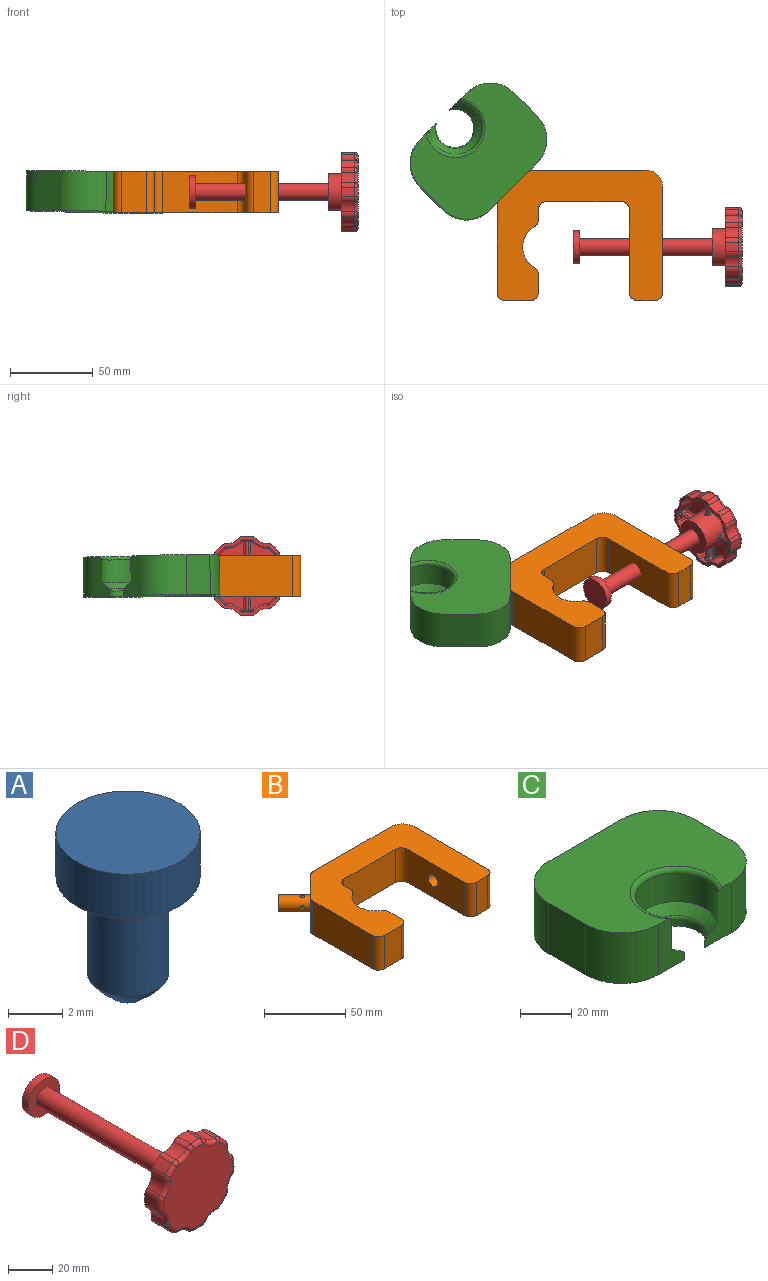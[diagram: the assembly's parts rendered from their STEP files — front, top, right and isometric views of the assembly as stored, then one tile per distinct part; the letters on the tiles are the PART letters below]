
ASSEMBLY  parts=4 mates=4
PART A: 6 faces, bbox 5.3x5.3x7.3 mm
  f0: cylinder r=1.5mm len=4.3mm, axis (0,0,-1), area 40.5mm2, adj f3,f5
  f1: cylinder r=2.65mm len=5.3mm, axis (0,0,-1), area 33.3mm2, adj f2,f3
  f2: plane 5.3x5.3mm, normal (0,0,1), area 22.1mm2, adj f1
  f3: plane 5.3x5.3mm, normal (0,0,-1), area 15mm2, adj f0,f1
  f4: plane 1.01x1.01mm, normal (0,0,-1), area 0.8mm2, adj f5
  f5: bspline ~3x3mm, area 9.3mm2, adj f0,f4
PART B: 35 faces, bbox 107.7x86.7x25 mm
  f0: cylinder r=5mm len=21.21mm, axis (0.71,-0.71,0), area 603.4mm2, adj f22,f23,f25,f27,f29,f31
  f1: plane 100x79mm, normal (0,0,-1), area 4176.6mm2, adj f2,f4,f5,f6,f7,f8,f9,f10
  f2: plane 51.93x25mm, normal (-1,0,0), area 1298.2mm2, adj f1,f3,f18,f34
  f3: plane 100x79mm, normal (0,0,1), area 4176.6mm2, adj f2,f4,f5,f6,f7,f8,f9,f10
  f4: plane 67.93x25mm, normal (0,1,0), area 1698.2mm2, adj f1,f3,f32,f33
  f5: plane 64x25mm, normal (1,0,0), area 1543.3mm2, adj f1,f3,f19,f21,f32
  f6: plane 25x10mm, normal (0,-1,0), area 250mm2, adj f1,f3,f20,f21
  f7: plane 25x15mm, normal (0,-1,0), area 375mm2, adj f1,f3,f17,f18
  f8: plane 50x25mm, normal (-1,0,0), area 1193.3mm2, adj f1,f3,f13,f19,f20
  f9: plane 45x25mm, normal (0,-1,0), area 1125mm2, adj f1,f3,f13,f14
  f10: plane 25x5.85mm, normal (1,0,0), area 146.2mm2, adj f1,f3,f14,f15
  f11: cylinder r=14.34mm len=25mm, axis (0,0,1), area 743.7mm2, adj f1,f3,f15,f16
  f12: plane 25x10.85mm, normal (1,0,0), area 271.2mm2, adj f1,f3,f16,f17
  f13: cylinder r=5mm len=25mm, axis (0,0,1), area 196.3mm2, adj f1,f3,f8,f9
  f14: cylinder r=5mm len=25mm, axis (0,0,1), area 196.3mm2, adj f1,f3,f9,f10
  f15: cylinder r=5mm len=25mm, axis (0,0,1), area 129.7mm2, adj f1,f3,f10,f11
  f16: cylinder r=5mm len=25mm, axis (0,0,1), area 129.7mm2, adj f1,f3,f11,f12
  f17: cylinder r=5mm len=25mm, axis (0,0,-1), area 196.3mm2, adj f1,f3,f7,f12
  f18: cylinder r=5mm len=25mm, axis (0,0,-1), area 196.3mm2, adj f1,f2,f3,f7
  f19: cylinder r=4.25mm len=20mm, axis (1,0,0), area 534.1mm2, adj f5,f8
  f20: cylinder r=5mm len=25mm, axis (0,0,1), area 196.3mm2, adj f1,f3,f6,f8
  f21: cylinder r=5mm len=25mm, axis (0,0,1), area 196.3mm2, adj f1,f3,f5,f6
  f22: plane 25x17.07mm, normal (-0.71,0.71,0), area 525mm2, adj f0,f1,f3,f33,f34
  f23: plane 10x7.07mm, normal (-0.71,0.71,0), area 78.5mm2, adj f0
  f24: plane 0.5x0.5mm, normal (0,0,1), area 0.2mm2, adj f25
  f25: bspline ~2.85x2.85mm, area 6.5mm2, adj f0,f24
  f26: plane 0.5x0.35mm, normal (-0.71,-0.71,0), area 0.2mm2, adj f27
  f27: bspline ~3.88x3.33mm, area 6.8mm2, adj f0,f26
  f28: plane 0.5x0.5mm, normal (0,0,-1), area 0.2mm2, adj f29
  f29: bspline ~2.96x2.96mm, area 6.8mm2, adj f0,f28
  f30: plane 0.5x0.36mm, normal (0.71,0.71,0), area 0.2mm2, adj f31
  f31: bspline ~2.96x2.11mm, area 7.9mm2, adj f0,f30
  f32: cylinder r=10mm len=25mm, axis (0,0,1), area 392.7mm2, adj f1,f3,f4,f5
  f33: cylinder r=5mm len=25mm, axis (0,0,1), area 98.2mm2, adj f1,f3,f4,f22
  f34: cylinder r=5mm len=25mm, axis (0,0,-1), area 98.2mm2, adj f1,f2,f3,f22
PART C: 21 faces, bbox 80x63.2x24 mm
  f0: cylinder r=1.65mm len=5.02mm, axis (0,0,-1), area 50.6mm2, adj f1,f20
  f1: cylinder r=5.25mm len=20mm, axis (0,1,0), area 651.1mm2, adj f0,f6,f16
  f2: plane 24x14.32mm, normal (0,-1,0), area 220.5mm2, adj f7,f8,f9,f10,f12,f13,f14,f15
  f3: plane 24x20mm, normal (-1,0,0), area 480mm2, adj f8,f12,f15,f17
  f4: plane 24x20mm, normal (1,0,0), area 480mm2, adj f8,f11,f15,f18
  f5: plane 24x14.32mm, normal (0,-1,0), area 220.5mm2, adj f7,f8,f9,f10,f11,f13,f14,f15
  f6: plane 40x24mm, normal (0,1,0), area 873.4mm2, adj f1,f8,f15,f17,f18
  f7: cylinder r=11.5mm len=23mm, axis (0,0,1), area 191.5mm2, adj f2,f5,f14,f15
  f8: plane 80x60mm, normal (0,0,1), area 3607.2mm2, adj f2,f3,f4,f5,f6,f11,f12,f13
  f9: cylinder r=16mm len=32mm, axis (0,0,1), area 970.2mm2, adj f2,f5,f10,f13
  f10: cone r=11.5mm half-angle=45deg, axis (0,0,1), area 368mm2, adj f2,f5,f9,f14
  f11: cylinder r=20mm len=24mm, axis (0,0,-1), area 754mm2, adj f4,f5,f8,f15
  f12: cylinder r=20mm len=24mm, axis (0,0,1), area 754mm2, adj f2,f3,f8,f15
  f13: torus R=18mm, axis (0,0,1), area 232.5mm2, adj f2,f5,f8,f9
  f14: torus R=13.5mm, axis (0,0,-1), area 95.4mm2, adj f2,f5,f7,f10
  f15: plane 80x60mm, normal (0,0,-1), area 4030.6mm2, adj f2,f3,f4,f5,f6,f7,f11,f12
  f16: plane 10.5x10.5mm, normal (0,1,0), area 86.6mm2, adj f1
  f17: cylinder r=20mm len=24mm, axis (0,0,-1), area 754mm2, adj f3,f6,f8,f15
  f18: cylinder r=20mm len=24mm, axis (0,0,1), area 754mm2, adj f4,f6,f8,f15
  f19: cylinder r=2.65mm len=5.3mm, axis (0,0,-1), area 33.3mm2, adj f15,f20
  f20: plane 5.3x5.3mm, normal (0,0,-1), area 13.5mm2, adj f0,f19
PART D: 219 faces, bbox 48.4x102x48.4 mm
  f0: plane 18.9x18.9mm, normal (0,1,0), area 169.4mm2, adj f128,f129,f130,f131,f132,f133,f134,f135
  f1: cylinder r=22mm len=7mm, axis (0,1,0), area 18.7mm2, adj f7,f92,f93,f135,f145,f171,f172,f173
  f2: cylinder r=22mm len=7mm, axis (0,1,0), area 18.7mm2, adj f7,f96,f97,f120,f136,f165,f166,f167
  f3: plane 18.9x18.9mm, normal (0,1,0), area 169.4mm2, adj f140,f141,f142,f143,f144,f145,f146,f147
  f4: cylinder r=22mm len=7mm, axis (0,1,0), area 18.7mm2, adj f7,f98,f99,f127,f159,f177,f178,f179
  f5: plane 18.9x18.9mm, normal (0,1,0), area 169.4mm2, adj f152,f153,f154,f155,f156,f157,f158,f159
  f6: cylinder r=22mm len=7mm, axis (0,1,0), area 18.7mm2, adj f7,f88,f89,f150,f160,f207,f208,f209
  f7: plane 48x48mm, normal (0,1,0), area 293.1mm2, adj f1,f2,f4,f6,f8,f9,f10,f11
  f8: cylinder r=8mm len=8mm, axis (0,1,0), area 58.9mm2, adj f7,f34,f35,f67
  f9: cylinder r=24mm len=8mm, axis (0,1,0), area 47.1mm2, adj f7,f33,f34,f63
  f10: cylinder r=8mm len=8mm, axis (0,1,0), area 58.9mm2, adj f7,f32,f33,f59
  f11: cylinder r=24mm len=8mm, axis (0,1,0), area 47.1mm2, adj f7,f31,f32,f55
  f12: cylinder r=8mm len=8mm, axis (0,1,0), area 58.9mm2, adj f7,f30,f31,f51
  f13: cylinder r=24mm len=8mm, axis (0,1,0), area 47.1mm2, adj f7,f29,f30,f47
  f14: cylinder r=8mm len=8mm, axis (0,1,0), area 58.9mm2, adj f7,f28,f29,f43
  f15: cylinder r=24mm len=8mm, axis (0,1,0), area 47.1mm2, adj f7,f27,f28,f42
  f16: cylinder r=8mm len=8mm, axis (0,1,0), area 58.9mm2, adj f7,f26,f27,f46
  f17: cylinder r=24mm len=8mm, axis (0,1,0), area 47.1mm2, adj f7,f25,f26,f50
  f18: cylinder r=8mm len=8mm, axis (0,1,0), area 58.9mm2, adj f7,f25,f37,f54
  f19: cylinder r=24mm len=8mm, axis (0,1,0), area 47.1mm2, adj f7,f37,f38,f58
  f20: cylinder r=8mm len=8mm, axis (0,1,0), area 58.9mm2, adj f7,f38,f39,f62
  f21: cylinder r=24mm len=8mm, axis (0,1,0), area 47.1mm2, adj f7,f39,f40,f66
  f22: cylinder r=8mm len=8mm, axis (0,1,0), area 58.9mm2, adj f7,f36,f40,f70
  f23: cylinder r=24mm len=8mm, axis (0,1,0), area 47.1mm2, adj f7,f35,f36,f71
  f24: plane 44x44mm, normal (0,-1,0), area 1411.4mm2, adj f41,f42,f43,f44,f45,f46,f47,f48
  f25: cylinder r=4mm len=8mm, axis (0,-1,0), area 23.4mm2, adj f7,f17,f18,f52
  f26: cylinder r=4mm len=8mm, axis (0,-1,0), area 23.4mm2, adj f7,f16,f17,f48
  f27: cylinder r=4mm len=8mm, axis (0,-1,0), area 23.4mm2, adj f7,f15,f16,f44
  f28: cylinder r=4mm len=8mm, axis (0,-1,0), area 23.4mm2, adj f7,f14,f15,f41
  f29: cylinder r=4mm len=8mm, axis (0,-1,0), area 23.4mm2, adj f7,f13,f14,f45
  f30: cylinder r=4mm len=8mm, axis (0,-1,0), area 23.4mm2, adj f7,f12,f13,f49
  f31: cylinder r=4mm len=8mm, axis (0,-1,0), area 23.4mm2, adj f7,f11,f12,f53
  f32: cylinder r=4mm len=8mm, axis (0,-1,0), area 23.4mm2, adj f7,f10,f11,f57
  f33: cylinder r=4mm len=8mm, axis (0,-1,0), area 23.4mm2, adj f7,f9,f10,f61
  f34: cylinder r=4mm len=8mm, axis (0,-1,0), area 23.4mm2, adj f7,f8,f9,f65
  f35: cylinder r=4mm len=8mm, axis (0,-1,0), area 23.4mm2, adj f7,f8,f23,f69
  f36: cylinder r=4mm len=8mm, axis (0,-1,0), area 23.4mm2, adj f7,f22,f23,f72
  f37: cylinder r=4mm len=8mm, axis (0,-1,0), area 23.4mm2, adj f7,f18,f19,f56
  f38: cylinder r=4mm len=8mm, axis (0,-1,0), area 23.4mm2, adj f7,f19,f20,f60
  f39: cylinder r=4mm len=8mm, axis (0,-1,0), area 23.4mm2, adj f7,f20,f21,f64
  f40: cylinder r=4mm len=8mm, axis (0,-1,0), area 23.4mm2, adj f7,f21,f22,f68
  f41: torus R=2mm, axis (0,1,0), area 7.5mm2, adj f24,f28,f42,f43
  f42: torus R=22mm, axis (0,1,0), area 18mm2, adj f15,f24,f41,f44
  f43: torus R=10mm, axis (0,1,0), area 25.3mm2, adj f14,f24,f41,f45
  f44: torus R=2mm, axis (0,1,0), area 7.5mm2, adj f24,f27,f42,f46
  f45: torus R=2mm, axis (0,1,0), area 7.5mm2, adj f24,f29,f43,f47
  f46: torus R=10mm, axis (0,1,0), area 25.3mm2, adj f16,f24,f44,f48
  f47: torus R=22mm, axis (0,1,0), area 18mm2, adj f13,f24,f45,f49
  f48: torus R=2mm, axis (0,1,0), area 7.5mm2, adj f24,f26,f46,f50
  f49: torus R=2mm, axis (0,1,0), area 7.5mm2, adj f24,f30,f47,f51
  f50: torus R=22mm, axis (0,1,0), area 18mm2, adj f17,f24,f48,f52
  f51: torus R=10mm, axis (0,1,0), area 25.3mm2, adj f12,f24,f49,f53
  f52: torus R=2mm, axis (0,1,0), area 7.5mm2, adj f24,f25,f50,f54
  f53: torus R=2mm, axis (0,1,0), area 7.5mm2, adj f24,f31,f51,f55
  f54: torus R=10mm, axis (0,1,0), area 25.3mm2, adj f18,f24,f52,f56
  f55: torus R=22mm, axis (0,1,0), area 18mm2, adj f11,f24,f53,f57
  f56: torus R=2mm, axis (0,1,0), area 7.5mm2, adj f24,f37,f54,f58
  f57: torus R=2mm, axis (0,1,0), area 7.5mm2, adj f24,f32,f55,f59
  f58: torus R=22mm, axis (0,1,0), area 18mm2, adj f19,f24,f56,f60
  f59: torus R=10mm, axis (0,1,0), area 25.3mm2, adj f10,f24,f57,f61
  f60: torus R=2mm, axis (0,1,0), area 7.5mm2, adj f24,f38,f58,f62
  f61: torus R=2mm, axis (0,1,0), area 7.5mm2, adj f24,f33,f59,f63
  f62: torus R=10mm, axis (0,1,0), area 25.3mm2, adj f20,f24,f60,f64
  f63: torus R=22mm, axis (0,1,0), area 18mm2, adj f9,f24,f61,f65
  f64: torus R=2mm, axis (0,1,0), area 7.5mm2, adj f24,f39,f62,f66
  f65: torus R=2mm, axis (0,1,0), area 7.5mm2, adj f24,f34,f63,f67
  f66: torus R=22mm, axis (0,1,0), area 18mm2, adj f21,f24,f64,f68
  f67: torus R=10mm, axis (0,1,0), area 25.3mm2, adj f8,f24,f65,f69
  f68: torus R=2mm, axis (0,1,0), area 7.5mm2, adj f24,f40,f66,f70
  f69: torus R=2mm, axis (0,1,0), area 7.5mm2, adj f24,f35,f67,f71
  f70: torus R=10mm, axis (0,1,0), area 25.3mm2, adj f22,f24,f68,f72
  f71: torus R=22mm, axis (0,1,0), area 18mm2, adj f23,f24,f69,f72
  f72: torus R=2mm, axis (0,1,0), area 7.5mm2, adj f24,f36,f70,f71
  f73: cylinder r=10mm len=8.21mm, axis (0,1,0), area 64.5mm2, adj f7,f95,f96,f132
  f74: cylinder r=22mm len=7mm, axis (0,1,0), area 37.8mm2, adj f7,f94,f95,f128
  f75: cylinder r=10mm len=8.21mm, axis (0,1,0), area 64.5mm2, adj f7,f93,f94,f131
  f76: cylinder r=10mm len=8.21mm, axis (0,1,0), area 64.5mm2, adj f7,f91,f92,f141
  f77: cylinder r=22mm len=7mm, axis (0,1,0), area 37.8mm2, adj f7,f90,f91,f142
  f78: cylinder r=10mm len=8.21mm, axis (0,1,0), area 64.5mm2, adj f7,f89,f90,f146
  f79: cylinder r=10mm len=8.21mm, axis (0,1,0), area 64.5mm2, adj f7,f87,f88,f156
  f80: cylinder r=22mm len=7mm, axis (0,1,0), area 37.8mm2, adj f7,f86,f87,f152
  f81: cylinder r=10mm len=8.21mm, axis (0,1,0), area 64.5mm2, adj f7,f86,f98,f155
  f82: cylinder r=10mm len=8.21mm, axis (0,1,0), area 64.5mm2, adj f7,f99,f100,f123
  f83: cylinder r=22mm len=7mm, axis (0,1,0), area 37.8mm2, adj f7,f100,f101,f119
  f84: cylinder r=10mm len=8.21mm, axis (0,1,0), area 64.5mm2, adj f7,f97,f101,f116
  f85: plane 18.9x18.9mm, normal (0,1,0), area 169.4mm2, adj f116,f117,f118,f119,f120,f121,f122,f123
  f86: cylinder r=2mm len=7mm, axis (0,-1,0), area 10.2mm2, adj f7,f80,f81,f153
  f87: cylinder r=2mm len=7mm, axis (0,-1,0), area 10.2mm2, adj f7,f79,f80,f154
  f88: cylinder r=2mm len=7mm, axis (0,-1,0), area 10.2mm2, adj f6,f7,f79,f158
  f89: cylinder r=2mm len=7mm, axis (0,-1,0), area 10.2mm2, adj f6,f7,f78,f148
  f90: cylinder r=2mm len=7mm, axis (0,-1,0), area 10.2mm2, adj f7,f77,f78,f144
  f91: cylinder r=2mm len=7mm, axis (0,-1,0), area 10.2mm2, adj f7,f76,f77,f140
  f92: cylinder r=2mm len=7mm, axis (0,-1,0), area 10.2mm2, adj f1,f7,f76,f143
  f93: cylinder r=2mm len=7mm, axis (0,-1,0), area 10.2mm2, adj f1,f7,f75,f133
  f94: cylinder r=2mm len=7mm, axis (0,-1,0), area 10.2mm2, adj f7,f74,f75,f129
  f95: cylinder r=2mm len=7mm, axis (0,-1,0), area 10.2mm2, adj f7,f73,f74,f130
  f96: cylinder r=2mm len=7mm, axis (0,-1,0), area 10.2mm2, adj f2,f7,f73,f134
  f97: cylinder r=2mm len=7mm, axis (0,-1,0), area 10.2mm2, adj f2,f7,f84,f118
  f98: cylinder r=2mm len=7mm, axis (0,-1,0), area 10.2mm2, adj f4,f7,f81,f157
  f99: cylinder r=2mm len=7mm, axis (0,-1,0), area 10.2mm2, adj f4,f7,f82,f125
  f100: cylinder r=2mm len=7mm, axis (0,-1,0), area 10.2mm2, adj f7,f82,f83,f121
  f101: cylinder r=2mm len=7mm, axis (0,-1,0), area 10.2mm2, adj f7,f83,f84,f117
  f102: plane 22x22mm, normal (0,1,0), area 301.6mm2, adj f103,f212
  f103: cylinder r=11mm len=22mm, axis (0,-1,0), area 977.8mm2, adj f102,f124,f139,f149,f163,f183,f184,f185
  f104: plane 9.07x3mm, normal (0,0,1), area 27.2mm2, adj f113,f162,f204,f207
  f105: plane 9.07x3mm, normal (0,0,-1), area 27.2mm2, adj f113,f151,f201,f210
  f106: plane 9.07x3mm, normal (-1,0,0), area 27.2mm2, adj f115,f126,f177,f186
  f107: plane 9.07x3mm, normal (1,0,0), area 27.2mm2, adj f115,f161,f180,f183
  f108: plane 9.07x3mm, normal (0,0,-1), area 27.2mm2, adj f112,f138,f165,f192
  f109: plane 9.07x3mm, normal (0,0,1), area 27.2mm2, adj f112,f122,f168,f189
  f110: plane 9.07x3mm, normal (1,0,0), area 27.2mm2, adj f114,f147,f171,f198
  f111: plane 9.07x3mm, normal (-1,0,0), area 27.2mm2, adj f114,f137,f174,f195
  f112: cylinder r=1mm len=9.17mm, axis (1,0,0), area 28.4mm2, adj f108,f109,f166,f167,f190,f191
  f113: cylinder r=1mm len=9.17mm, axis (-1,0,0), area 28.4mm2, adj f104,f105,f202,f203,f208,f209
  f114: cylinder r=1mm len=9.17mm, axis (0,0,1), area 28.4mm2, adj f110,f111,f172,f173,f196,f197
  f115: cylinder r=1mm len=9.17mm, axis (0,0,-1), area 28.4mm2, adj f106,f107,f178,f179,f184,f185
  f116: torus R=11mm, axis (0,1,0), area 15mm2, adj f84,f85,f117,f118
  f117: torus R=1mm, axis (0,1,0), area 1.9mm2, adj f85,f101,f116,f119
  f118: torus R=1mm, axis (0,1,0), area 1.9mm2, adj f85,f97,f116,f120
  f119: torus R=21mm, axis (0,1,0), area 8.3mm2, adj f83,f85,f117,f121
  f120: torus R=21mm, axis (0,1,0), area 0.9mm2, adj f2,f85,f118,f169
  f121: torus R=1mm, axis (0,1,0), area 1.9mm2, adj f85,f100,f119,f123
  f122: cylinder r=1mm len=9.07mm, axis (-1,0,0), area 14.3mm2, adj f85,f109,f169,f188
  f123: torus R=11mm, axis (0,1,0), area 15mm2, adj f82,f85,f121,f125
  f124: torus R=12mm, axis (0,1,0), area 22.1mm2, adj f85,f103,f187,f188
  f125: torus R=1mm, axis (0,1,0), area 1.9mm2, adj f85,f99,f123,f127
  f126: cylinder r=1mm len=9.07mm, axis (0,0,-1), area 14.3mm2, adj f85,f106,f176,f187
  f127: torus R=21mm, axis (0,1,0), area 0.9mm2, adj f4,f85,f125,f176
  f128: torus R=21mm, axis (0,1,0), area 8.3mm2, adj f0,f74,f129,f130
  f129: torus R=1mm, axis (0,1,0), area 1.9mm2, adj f0,f94,f128,f131
  f130: torus R=1mm, axis (0,1,0), area 1.9mm2, adj f0,f95,f128,f132
  f131: torus R=11mm, axis (0,1,0), area 15mm2, adj f0,f75,f129,f133
  f132: torus R=11mm, axis (0,1,0), area 15mm2, adj f0,f73,f130,f134
  f133: torus R=1mm, axis (0,1,0), area 1.9mm2, adj f0,f93,f131,f135
  f134: torus R=1mm, axis (0,1,0), area 1.9mm2, adj f0,f96,f132,f136
  f135: torus R=21mm, axis (0,1,0), area 0.9mm2, adj f0,f1,f133,f175
  f136: torus R=21mm, axis (0,1,0), area 0.9mm2, adj f0,f2,f134,f164
  f137: cylinder r=1mm len=9.07mm, axis (0,0,1), area 14.3mm2, adj f0,f111,f175,f194
  f138: cylinder r=1mm len=9.07mm, axis (-1,0,0), area 14.3mm2, adj f0,f108,f164,f193
  f139: torus R=12mm, axis (0,1,0), area 22.1mm2, adj f0,f103,f193,f194
  f140: torus R=1mm, axis (0,1,0), area 1.9mm2, adj f3,f91,f141,f142
  f141: torus R=11mm, axis (0,1,0), area 15mm2, adj f3,f76,f140,f143
  f142: torus R=21mm, axis (0,1,0), area 8.3mm2, adj f3,f77,f140,f144
  f143: torus R=1mm, axis (0,1,0), area 1.9mm2, adj f3,f92,f141,f145
  f144: torus R=1mm, axis (0,1,0), area 1.9mm2, adj f3,f90,f142,f146
  f145: torus R=21mm, axis (0,1,0), area 0.9mm2, adj f1,f3,f143,f170
  f146: torus R=11mm, axis (0,1,0), area 15mm2, adj f3,f78,f144,f148
  f147: cylinder r=1mm len=9.07mm, axis (0,0,-1), area 14.3mm2, adj f3,f110,f170,f199
  f148: torus R=1mm, axis (0,1,0), area 1.9mm2, adj f3,f89,f146,f150
  f149: torus R=12mm, axis (0,1,0), area 22.1mm2, adj f3,f103,f199,f200
  f150: torus R=21mm, axis (0,1,0), area 0.9mm2, adj f3,f6,f148,f211
  f151: cylinder r=1mm len=9.07mm, axis (-1,0,0), area 14.3mm2, adj f3,f105,f200,f211
  f152: torus R=21mm, axis (0,1,0), area 8.3mm2, adj f5,f80,f153,f154
  f153: torus R=1mm, axis (0,1,0), area 1.9mm2, adj f5,f86,f152,f155
  f154: torus R=1mm, axis (0,1,0), area 1.9mm2, adj f5,f87,f152,f156
  f155: torus R=11mm, axis (0,1,0), area 15mm2, adj f5,f81,f153,f157
  f156: torus R=11mm, axis (0,1,0), area 15mm2, adj f5,f79,f154,f158
  f157: torus R=1mm, axis (0,1,0), area 1.9mm2, adj f5,f98,f155,f159
  f158: torus R=1mm, axis (0,1,0), area 1.9mm2, adj f5,f88,f156,f160
  f159: torus R=21mm, axis (0,1,0), area 0.9mm2, adj f4,f5,f157,f181
  f160: torus R=21mm, axis (0,1,0), area 0.9mm2, adj f5,f6,f158,f206
  f161: cylinder r=1mm len=9.07mm, axis (0,0,1), area 14.3mm2, adj f5,f107,f181,f182
  f162: cylinder r=1mm len=9.07mm, axis (-1,0,0), area 14.3mm2, adj f5,f104,f205,f206
  f163: torus R=12mm, axis (0,1,0), area 22.1mm2, adj f5,f103,f182,f205
  f164: sphere r=1mm, area 1.7mm2, adj f136,f138,f165
  f165: cylinder r=1mm len=3mm, axis (0,1,0), area 5mm2, adj f2,f108,f164,f166
  f166: bspline ~2.1x2mm, area 3.5mm2, adj f2,f112,f165,f167
  f167: bspline ~2.1x2mm, area 3.5mm2, adj f2,f112,f166,f168
  f168: cylinder r=1mm len=3mm, axis (0,1,0), area 5mm2, adj f2,f109,f167,f169
  f169: sphere r=1mm, area 2.4mm2, adj f120,f122,f168
  f170: sphere r=1mm, area 2.4mm2, adj f145,f147,f171
  f171: cylinder r=1mm len=3mm, axis (0,1,0), area 5mm2, adj f1,f110,f170,f172
  f172: bspline ~2.1x2mm, area 3.5mm2, adj f1,f114,f171,f173
  f173: bspline ~2.1x2mm, area 3.5mm2, adj f1,f114,f172,f174
  f174: cylinder r=1mm len=3mm, axis (0,1,0), area 5mm2, adj f1,f111,f173,f175
  f175: sphere r=1mm, area 1.3mm2, adj f135,f137,f174
  f176: sphere r=1mm, area 1.2mm2, adj f126,f127,f177
  f177: cylinder r=1mm len=3mm, axis (0,1,0), area 5mm2, adj f4,f106,f176,f178
  f178: bspline ~2.1x2mm, area 3.5mm2, adj f4,f115,f177,f179
  f179: bspline ~2.1x2mm, area 3.5mm2, adj f4,f115,f178,f180
  f180: cylinder r=1mm len=3mm, axis (0,1,0), area 5mm2, adj f4,f107,f179,f181
  f181: sphere r=1mm, area 1.7mm2, adj f159,f161,f180
  f182: sphere r=1mm, area 0.9mm2, adj f161,f163,f183
  f183: cylinder r=1mm len=3mm, axis (0,-1,0), area 4.2mm2, adj f103,f107,f182,f184
  f184: bspline ~2x1.83mm, area 3.1mm2, adj f103,f115,f183,f185
  f185: bspline ~2x1.83mm, area 3.1mm2, adj f103,f115,f184,f186
  f186: cylinder r=1mm len=3mm, axis (0,-1,0), area 4.2mm2, adj f103,f106,f185,f187
  f187: sphere r=1mm, area 1.4mm2, adj f124,f126,f186
  f188: sphere r=1mm, area 0.9mm2, adj f122,f124,f189
  f189: cylinder r=1mm len=3mm, axis (0,-1,0), area 4.2mm2, adj f103,f109,f188,f190
  f190: bspline ~2x1.83mm, area 3.1mm2, adj f103,f112,f189,f191
  f191: bspline ~2x1.83mm, area 3.1mm2, adj f103,f112,f190,f192
  f192: cylinder r=1mm len=3mm, axis (0,-1,0), area 4.2mm2, adj f103,f108,f191,f193
  f193: sphere r=1mm, area 0.9mm2, adj f138,f139,f192
  f194: sphere r=1mm, area 1.4mm2, adj f137,f139,f195
  f195: cylinder r=1mm len=3mm, axis (0,-1,0), area 4.2mm2, adj f103,f111,f194,f196
  f196: bspline ~2x1.83mm, area 3.1mm2, adj f103,f114,f195,f197
  f197: bspline ~2x1.83mm, area 3.1mm2, adj f103,f114,f196,f198
  f198: cylinder r=1mm len=3mm, axis (0,-1,0), area 4.2mm2, adj f103,f110,f197,f199
  f199: sphere r=1mm, area 0.9mm2, adj f147,f149,f198
  f200: sphere r=1mm, area 1.4mm2, adj f149,f151,f201
  f201: cylinder r=1mm len=3mm, axis (0,-1,0), area 4.2mm2, adj f103,f105,f200,f202
  f202: bspline ~2x1.83mm, area 3.1mm2, adj f103,f113,f201,f203
  f203: bspline ~2x1.83mm, area 3.1mm2, adj f103,f113,f202,f204
  f204: cylinder r=1mm len=3mm, axis (0,-1,0), area 4.2mm2, adj f103,f104,f203,f205
  f205: sphere r=1mm, area 0.9mm2, adj f162,f163,f204
  f206: sphere r=1mm, area 1.3mm2, adj f160,f162,f207
  f207: cylinder r=1mm len=3mm, axis (0,1,0), area 5mm2, adj f6,f104,f206,f208
  f208: bspline ~2.1x2mm, area 3.5mm2, adj f6,f113,f207,f209
  f209: bspline ~2.1x2mm, area 3.5mm2, adj f6,f113,f208,f210
  f210: cylinder r=1mm len=3mm, axis (0,1,0), area 5mm2, adj f6,f105,f209,f211
  f211: sphere r=1mm, area 1.2mm2, adj f150,f151,f210
  f212: cylinder r=5mm len=80mm, axis (0,-1,0), area 2513.3mm2, adj f102,f213
  f213: plane 20x20mm, normal (0,-1,0), area 235.6mm2, adj f212,f215
  f214: plane 20x20mm, normal (0,1,0), area 314.2mm2, adj f215
  f215: cylinder r=10mm len=20mm, axis (0,-1,0), area 251.3mm2, adj f213,f214
  f216: cone r=0mm half-angle=59deg, axis (0,1,0), area 5.7mm2, adj f217
  f217: cylinder r=1.25mm len=6.5mm, axis (0,1,0), area 51.1mm2, adj f216,f218
  f218: plane 2.5x2.5mm, normal (0,-1,0), area 4.9mm2, adj f217
PLACE A rot(axis=(0.38,-0.92,0),178.9deg) t=(87.42,60.29,-33.87)mm
PLACE B t=(119.88,-11.18,-40.84)mm fixed
PLACE C rot(axis=(-0.01,0,-1),135deg) t=(194.63,173.02,45.14)mm
PLACE D rot(axis=(-0.58,0.58,0.58),120deg) t=(106.56,7.94,-28.34)mm
MATE cylindrical C.f1 <-> B.f0  axis (0.71,-0.71,0) through (83.56,61.94,-28.34)mm
MATE planar C.f1 <-> B.f0  axis (0.71,-0.71,0) through (83.56,61.94,-28.34)mm
MATE slider D.f1 <-> B.f19  axis (1,0,0) through (163.56,25.44,-28.34)mm
MATE fastened A.f0 <-> C.f0  axis (0.01,0.01,1) through (79.87,65.33,-38.34)mm
